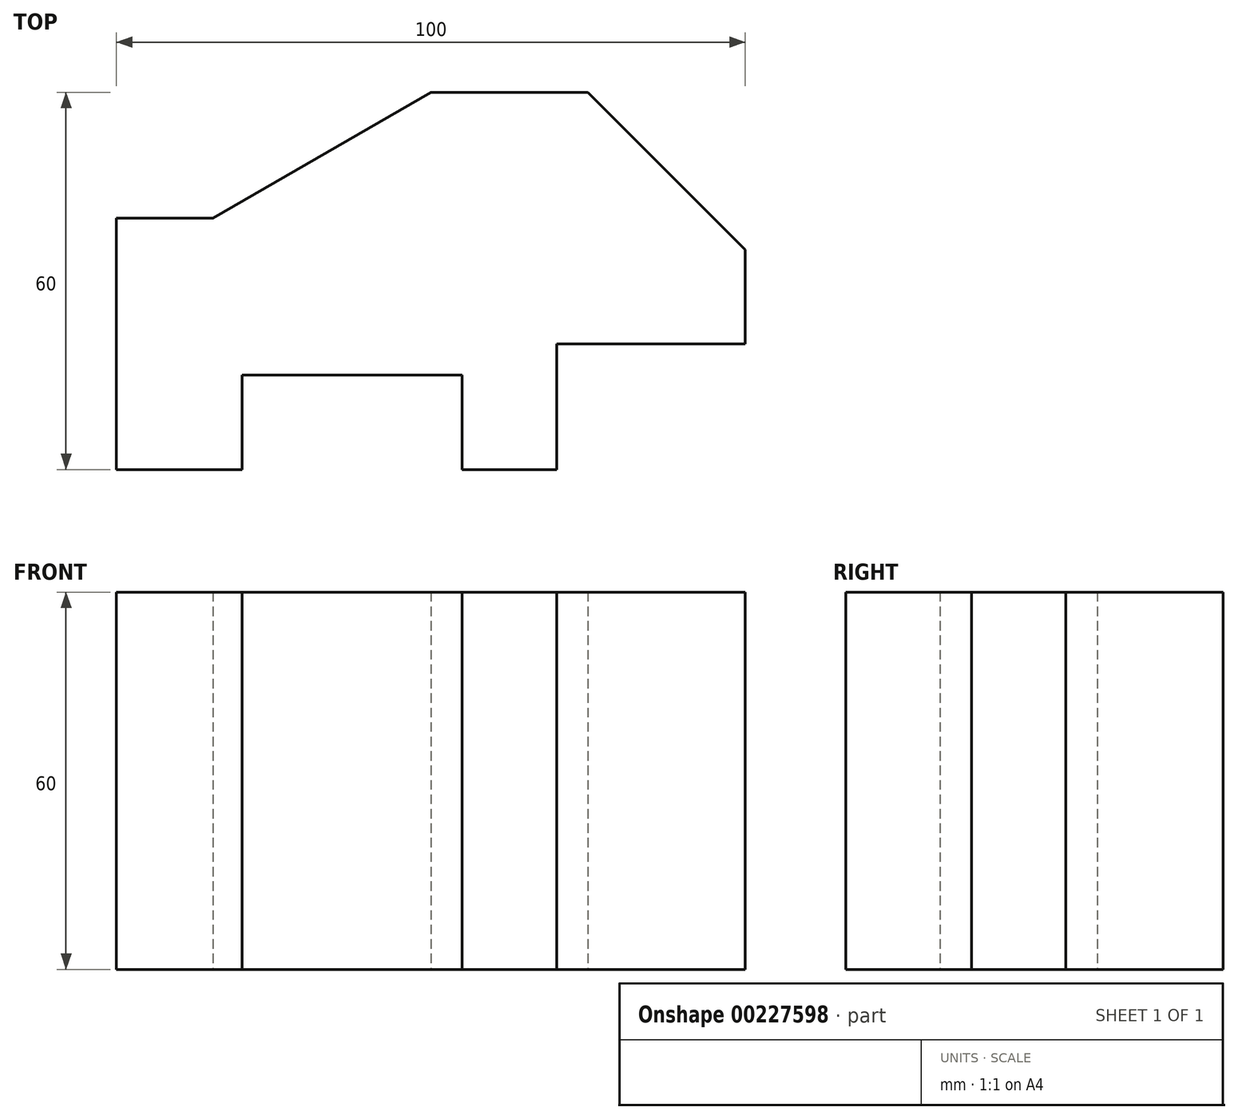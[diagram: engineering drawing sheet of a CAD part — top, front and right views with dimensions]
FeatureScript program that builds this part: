
annotation { "Feature Type Name" : "Feature", "Feature Type Description" : "" }
export const myFeature = defineFeature(function(context is Context, id is Id, definition is map)
    precondition{}
    {
        {
            var Q0;
            Q0=qCreatedBy(makeId("Top.planeOp"),FACE);
            var sketch = newSketch(context, id + "F0", { "sketchPlane" : qUnion([Q0])});
            skLineSegment(sketch, "E0", {"start": v(-33.4, 42.54) * mm, "end": v(-33.4, -17.46) * mm});
            skLineSegment(sketch, "E1", {"start": v(-33.4, -17.46) * mm, "end": v(-13.4, -17.46) * mm});
            skLineSegment(sketch, "E2", {"start": v(-13.4, -17.46) * mm, "end": v(-13.4, -2.46) * mm});
            skLineSegment(sketch, "E3", {"start": v(-13.4, -2.46) * mm, "end": v(21.6, -2.46) * mm});
            skLineSegment(sketch, "E4", {"start": v(21.6, -2.46) * mm, "end": v(21.6, -17.46) * mm});
            skLineSegment(sketch, "E5", {"start": v(21.6, -17.46) * mm, "end": v(36.6, -17.46) * mm});
            skLineSegment(sketch, "E6", {"start": v(36.6, -17.46) * mm, "end": v(36.6, 2.54) * mm});
            skLineSegment(sketch, "E7", {"start": v(36.6, 2.54) * mm, "end": v(66.6, 2.54) * mm});
            skLineSegment(sketch, "E8", {"start": v(66.6, 2.54) * mm, "end": v(66.6, 42.54) * mm});
            skLineSegment(sketch, "E9", {"start": v(66.6, 42.54) * mm, "end": v(-33.4, 42.54) * mm});
            skSolve(sketch);
        }
        {
            var Q0;
            Q0=makeQuery(id+"F0.imprint","IMPRINT",FACE,{"disambiguationData":[TD([[makeQuery(id+"F0.imprint","IMPRINT",EDGE,{"derivedFrom":sQuery(id+"F0.wireOp",EDGE,"E0")}),1.0]])]});
            extrude(context, id + "F1", {"entities" : qUnion([Q0]), "depth" : 60 * mm});
        }
        {
            var Q0;
            Q0=qCreatedBy(makeId("Top.planeOp"),FACE);
            var sketch = newSketch(context, id + "F2", { "sketchPlane" : qUnion([Q0])});
            skLineSegment(sketch, "E10.0.1", {"start": v(66.6, 42.54) * mm, "end": v(41.6, 42.54) * mm});
            skLineSegment(sketch, "E10.0.2", {"start": v(-33.4, 42.54) * mm, "end": v(-33.4, -17.46) * mm});
            skLineSegment(sketch, "E10.0.3", {"start": v(-33.4, -17.46) * mm, "end": v(-13.4, -17.46) * mm});
            skLineSegment(sketch, "E10.0.7", {"start": v(21.6, -17.46) * mm, "end": v(36.6, -17.46) * mm});
            skLineSegment(sketch, "E10.0.8", {"start": v(36.6, -17.46) * mm, "end": v(36.6, 2.54) * mm});
            skLineSegment(sketch, "E10.0.9", {"start": v(36.6, 2.54) * mm, "end": v(66.6, 2.54) * mm});
            skLineSegment(sketch, "E11.0.0", {"start": v(66.6, 17.54) * mm, "end": v(66.6, 42.54) * mm, "construction": true});
            skLineSegment(sketch, "E11.0.1", {"start": v(66.6, 42.54) * mm, "end": v(41.6, 42.54) * mm, "construction": true});
            skLineSegment(sketch, "E11.0.2", {"start": v(-33.4, 42.54) * mm, "end": v(-33.4, -17.46) * mm, "construction": true});
            skLineSegment(sketch, "E12.0.2", {"start": v(-33.4, 42.54) * mm, "end": v(-33.4, 22.54) * mm, "construction": true});
            skLineSegment(sketch, "E12.0.3", {"start": v(-33.4, -17.46) * mm, "end": v(-13.4, -17.46) * mm, "construction": true});
            skLineSegment(sketch, "E13", {"start": v(-18.04, 22.54) * mm, "end": v(16.6, 42.54) * mm});
            skLineSegment(sketch, "E14", {"start": v(16.6, 42.54) * mm, "end": v(-33.4, 42.54) * mm});
            skLineSegment(sketch, "E15", {"start": v(-33.4, 42.54) * mm, "end": v(-33.4, 23.58) * mm});
            skLineSegment(sketch, "E16", {"start": v(41.6, 42.54) * mm, "end": v(66.6, 17.54) * mm});
            skLineSegment(sketch, "E17", {"start": v(66.6, 17.54) * mm, "end": v(66.6, 42.54) * mm});
            skLineSegment(sketch, "E18", {"start": v(-18.04, 22.54) * mm, "end": v(-33.4, 22.54) * mm});
            skLineSegment(sketch, "E19.trimOffspring", {"start": v(16.6, 42.54) * mm, "end": v(-33.4, 42.54) * mm, "construction": true});
            skSolve(sketch);
        }
        {
            var Q0;
            Q0 = qSketchRegion(id + "F2", true);
            extrude(context, id + "F3", {"entities" : qUnion([Q0]), "operationType" : NewBodyOperationType.ADD, "depth" : 25 * mm});
        }
        {
            var Q0;
            Q0=makeQuery(id+"F2.imprint","IMPRINT",FACE,{"disambiguationData":[TD([[makeQuery(id+"F2.imprint","IMPRINT",EDGE,{"derivedFrom":sQuery(id+"F2.wireOp",EDGE,"E10.0.1")}),1.0]])]});
            var Q1;
            Q1=makeQuery(id+"F2.imprint","IMPRINT",FACE,{"disambiguationData":[TD([[makeQuery(id+"F2.imprint","IMPRINT",EDGE,{"derivedFrom":sQuery(id+"F2.wireOp",EDGE,"E13")}),1.0]])]});
            extrude(context, id + "F4", {"entities" : qUnion([Q0, Q1]), "operationType" : NewBodyOperationType.REMOVE, "depth" : 78 * mm});
        }
    });
